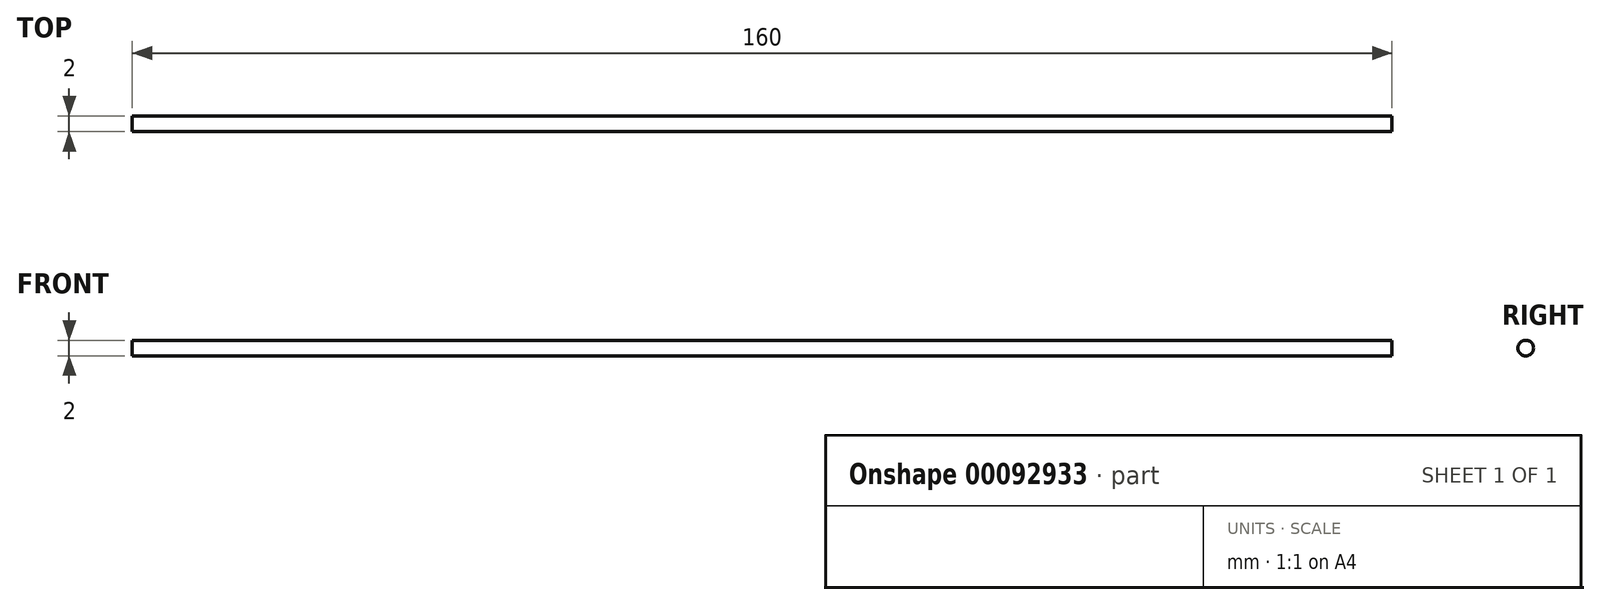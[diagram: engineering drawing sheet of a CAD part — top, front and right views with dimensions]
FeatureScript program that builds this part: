
annotation { "Feature Type Name" : "Feature", "Feature Type Description" : "" }
export const myFeature = defineFeature(function(context is Context, id is Id, definition is map)
    precondition{}
    {
        {
            var Q0;
            Q0=qCreatedBy(makeId("Front.planeOp"),FACE);
            var sketch = newSketch(context, id + "F0", { "sketchPlane" : qUnion([Q0])});
            skLineSegment(sketch, "E0", {"start": v(0, 0) * mm, "end": v(-160, 0) * mm});
            skSolve(sketch);
        }
        {
            var Q0;
            Q0=qCreatedBy(makeId("Right.planeOp"),FACE);
            var sketch = newSketch(context, id + "F1", { "sketchPlane" : qUnion([Q0])});
            skCircle(sketch, "E1", {"center": v(0, 0) * mm, "radius": 1 * mm});
            skSolve(sketch);
        }
        {
            var Q0;
            Q0 = qSketchRegion(id + "F1", true);
            var Q1;
            Q1 = qConstructionFilter(qBodyType(qCreatedBy(id + "F0" ,EDGE), BodyType.WIRE), ConstructionObject.NO);
            sweep(context, id + "F2", {"profiles" : qUnion([Q0]), "path" : qUnion([Q1])});
        }
    });
